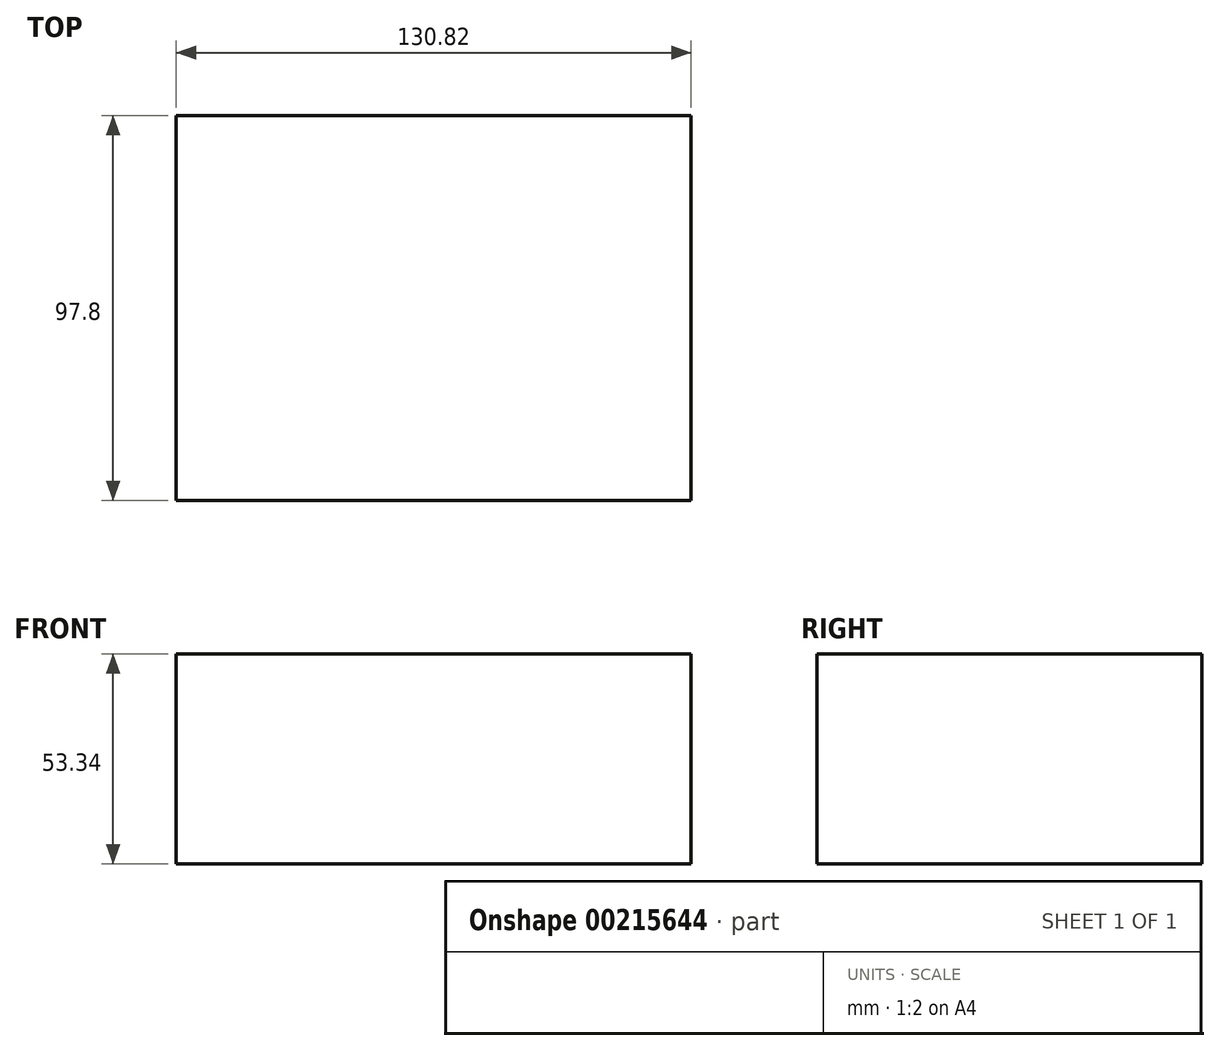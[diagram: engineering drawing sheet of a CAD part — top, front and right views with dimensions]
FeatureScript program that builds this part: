
annotation { "Feature Type Name" : "Feature", "Feature Type Description" : "" }
export const myFeature = defineFeature(function(context is Context, id is Id, definition is map)
    precondition{}
    {
        {
            var Q0;
            Q0=qCreatedBy(makeId("Top.planeOp"),FACE);
            var sketch = newSketch(context, id + "F0", { "sketchPlane" : qUnion([Q0])});
            skLineSegment(sketch, "E0.bottom", {"start": v(65.4, -48.9) * mm, "end": v(-65.4, -48.9) * mm});
            skLineSegment(sketch, "E0.top", {"start": v(65.4, 48.9) * mm, "end": v(-65.4, 48.9) * mm});
            skLineSegment(sketch, "E0.left", {"start": v(65.4, -48.9) * mm, "end": v(65.4, 48.9) * mm});
            skLineSegment(sketch, "E0.right", {"start": v(-65.4, -48.9) * mm, "end": v(-65.4, 48.9) * mm});
            skPoint(sketch, "E0.middle", {"position": v(0, 0) * mm});
            skSolve(sketch);
        }
        {
            var Q0;
            Q0 = qSketchRegion(id + "F0", true);
            extrude(context, id + "F1", {"entities" : qUnion([Q0]), "depth" : 53.34 * mm});
        }
    });
